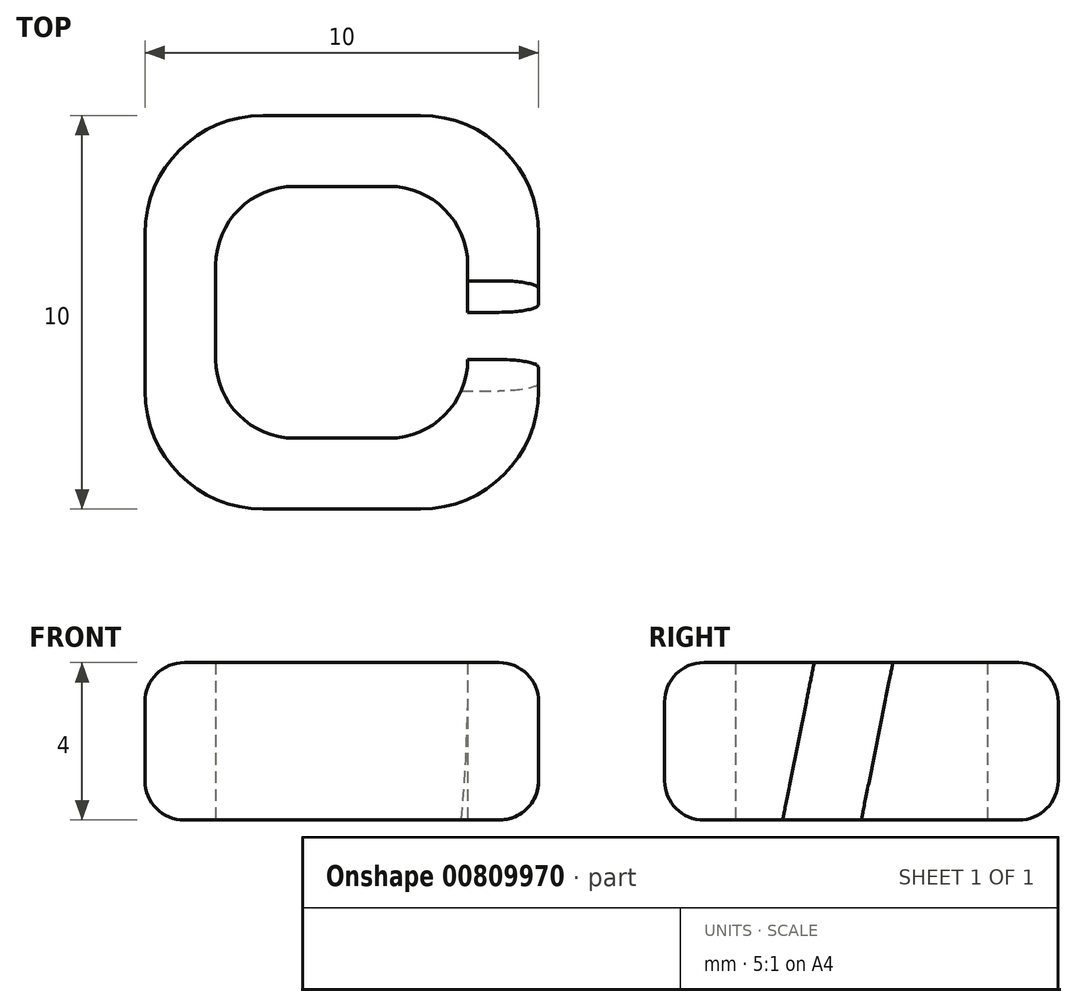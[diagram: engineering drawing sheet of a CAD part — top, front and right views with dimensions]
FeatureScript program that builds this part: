
annotation { "Feature Type Name" : "Feature", "Feature Type Description" : "" }
export const myFeature = defineFeature(function(context is Context, id is Id, definition is map)
    precondition{}
    {
        {
            var Q0;
            Q0=qCreatedBy(makeId("Top.planeOp"),FACE);
            var sketch = newSketch(context, id + "F0", { "sketchPlane" : qUnion([Q0])});
            skLineSegment(sketch, "E0.bottom", {"start": v(-5, 5) * mm, "end": v(5, 5) * mm});
            skLineSegment(sketch, "E0.top", {"start": v(-5, -5) * mm, "end": v(5, -5) * mm});
            skLineSegment(sketch, "E0.left", {"start": v(-5, 5) * mm, "end": v(-5, -5) * mm});
            skLineSegment(sketch, "E0.right", {"start": v(5, 5) * mm, "end": v(5, -5) * mm});
            skPoint(sketch, "E0.middle", {"position": v(0, 0) * mm});
            skSolve(sketch);
        }
        {
            var Q0;
            Q0=makeQuery(id+"F0.imprint","IMPRINT",FACE,{"disambiguationData":[TD([[makeQuery(id+"F0.imprint","IMPRINT",EDGE,{"derivedFrom":sQuery(id+"F0.wireOp",EDGE,"E0.bottom")}),-1.0]])]});
            extrude(context, id + "F1", {"entities" : qUnion([Q0]), "depth" : 4 * mm, "offsetDistance" : 25 * mm});
        }
        {
            var Q0;
            Q0=makeQuery(id+"F1.opExtrude","CAP_FACE",FACE,{"disambiguationData":[OSD([sQuery(id+"F0.wireOp",EDGE,"E0.bottom"),sQuery(id+"F0.wireOp",EDGE,"E0.top"),sQuery(id+"F0.wireOp",EDGE,"E0.left"),sQuery(id+"F0.wireOp",EDGE,"E0.right")])],"isStart":false});
            var Q1;
            Q1=makeQuery(id+"F1.opExtrude","CAP_FACE",FACE,{"disambiguationData":[OSD([sQuery(id+"F0.wireOp",EDGE,"E0.bottom"),sQuery(id+"F0.wireOp",EDGE,"E0.top"),sQuery(id+"F0.wireOp",EDGE,"E0.left"),sQuery(id+"F0.wireOp",EDGE,"E0.right")])],"isStart":true});
            shell(context, id + "F2", {"entities" : qUnion([Q0, Q1]), "thickness" : 1.8 * mm});
        }
        {
            var Q0;
            Q0=qCreatedBy(makeId("Right.planeOp"),FACE);
            cPlane(context, id + "F3", {"entities" : qUnion([Q0]), "cplaneType" : CPlaneType.OFFSET, "offset" : 5 * mm, "width" : 150 * mm, "height" : 150 * mm});
        }
        {
            var Q0;
            Q0=qCreatedBy(id+"F3.planeOp",FACE);
            var sketch = newSketch(context, id + "F4", { "sketchPlane" : qUnion([Q0])});
            skLineSegment(sketch, "E1.bottom", {"start": v(0, 0) * mm, "end": v(-5, 0) * mm});
            skLineSegment(sketch, "E1.top", {"start": v(0, 10) * mm, "end": v(-5, 10) * mm});
            skLineSegment(sketch, "E1.right", {"start": v(-5, 0) * mm, "end": v(-5, 10) * mm});
            skLineSegment(sketch, "E2.bottom", {"start": v(0, 0) * mm, "end": v(5, 0) * mm});
            skLineSegment(sketch, "E2.top", {"start": v(0, 10) * mm, "end": v(5, 10) * mm});
            skLineSegment(sketch, "E2.right", {"start": v(5, 0) * mm, "end": v(5, 10) * mm});
            skLineSegment(sketch, "E3", {"start": v(5, 10) * mm, "end": v(2, 10) * mm});
            skLineSegment(sketch, "E4", {"start": v(-5, 0) * mm, "end": v(-2, 0) * mm});
            skLineSegment(sketch, "E5", {"start": v(-2, 0) * mm, "end": v(0, 10) * mm});
            skLineSegment(sketch, "E6", {"start": v(0, 0) * mm, "end": v(2, 10) * mm});
            skSolve(sketch);
        }
        {
            var Q0;
            {var subQ0=sQuery(id+"F4.wireOp",EDGE,"E5");Q0=makeQuery(id+"F4.imprint","IMPRINT",FACE,{"disambiguationData":[TD([[makeQuery(id+"F4.imprint","IMPRINT",EDGE,{"derivedFrom":subQ0}),-1.0]])]});}
            extrude(context, id + "F5", {"entities" : qUnion([Q0]), "operationType" : NewBodyOperationType.REMOVE, "oppositeDirection" : true, "depth" : 1.8 * mm, "offsetDistance" : 25 * mm});
        }
        {
            var Q0;
            Q0=makeQuery(id+"F1.opExtrude","SWEPT_EDGE",EDGE,{"disambiguationData":[OSD([sQuery(id+"F0.wireOp",EDGE,"E0.top"),sQuery(id+"F0.wireOp",EDGE,"E0.right")])]});
            var Q1;
            Q1=makeQuery(id+"F1.opExtrude","SWEPT_EDGE",EDGE,{"disambiguationData":[OSD([sQuery(id+"F0.wireOp",EDGE,"E0.bottom"),sQuery(id+"F0.wireOp",EDGE,"E0.left")])]});
            var Q2;
            Q2=makeQuery(id+"F1.opExtrude","SWEPT_EDGE",EDGE,{"disambiguationData":[OSD([sQuery(id+"F0.wireOp",EDGE,"E0.bottom"),sQuery(id+"F0.wireOp",EDGE,"E0.right")])]});
            var Q3;
            Q3=makeQuery(id+"F1.opExtrude","SWEPT_EDGE",EDGE,{"disambiguationData":[OSD([sQuery(id+"F0.wireOp",EDGE,"E0.top"),sQuery(id+"F0.wireOp",EDGE,"E0.left")])]});
            fillet(context, id + "F6", {"entities" : qUnion([Q0, Q1, Q2, Q3]), "radius" : 3 * mm, "tangentPropagation" : true, "allowEdgeOverflow" : false});
        }
        {
            var Q0;
            Q0=makeQuery(id+"F1.opExtrude","CAP_EDGE",EDGE,{"disambiguationData":[OSD([sQuery(id+"F0.wireOp",EDGE,"E0.top")])],"isStart":false});
            var Q1;
            Q1=makeQuery(id+"F1.opExtrude","CAP_EDGE",EDGE,{"disambiguationData":[OSD([sQuery(id+"F0.wireOp",EDGE,"E0.left")])],"isStart":true});
            fillet(context, id + "F7", {"entities" : qUnion([Q0, Q1]), "radius" : 1 * mm, "tangentPropagation" : true, "allowEdgeOverflow" : false});
        }
        {
            var Q0;
            Q0=makeQuery(id+"F2.opShell","OFFSET_EDGE",EDGE,{"disambiguationData":[OSD([sQuery(id+"F0.wireOp",EDGE,"E0.bottom"),sQuery(id+"F0.wireOp",EDGE,"E0.right")])]});
            var Q1;
            Q1=makeQuery(id+"F2.opShell","OFFSET_EDGE",EDGE,{"disambiguationData":[OSD([sQuery(id+"F0.wireOp",EDGE,"E0.bottom"),sQuery(id+"F0.wireOp",EDGE,"E0.left")])]});
            var Q2;
            Q2=makeQuery(id+"F2.opShell","OFFSET_EDGE",EDGE,{"disambiguationData":[OSD([sQuery(id+"F0.wireOp",EDGE,"E0.top"),sQuery(id+"F0.wireOp",EDGE,"E0.right")])]});
            var Q3;
            Q3=makeQuery(id+"F2.opShell","OFFSET_EDGE",EDGE,{"disambiguationData":[OSD([sQuery(id+"F0.wireOp",EDGE,"E0.top"),sQuery(id+"F0.wireOp",EDGE,"E0.left")])]});
            fillet(context, id + "F8", {"entities" : qUnion([Q0, Q1, Q2, Q3]), "radius" : 2 * mm, "tangentPropagation" : true, "allowEdgeOverflow" : false});
        }
    });
